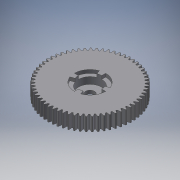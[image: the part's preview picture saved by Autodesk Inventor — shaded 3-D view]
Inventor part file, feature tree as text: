
AUTODESK INVENTOR PART (.ipt)
format: ipt  version: 2017 (Build 210142000, 142)  size: 384,000 bytes
history: native  units: mm
features: extrude x5, sketch x4, pattern_circular x2
ambient origin geometry x8: Origin, YZ Plane, XZ Plane, XY Plane, X Axis, Y Axis, Z Axis, Center Point
bodies: Solid1 (feature_tree)
feature tree (11):
  sketch  "Sketch1"  dims[d0=20.0mm d1=0.0mm]
  extrude  "Extrusion1"  TaperAngle=0.0deg  [1 undecoded]
  extrude  "Extrusion2"  Depth=10.0mm TaperAngle=360.0deg
  pattern_circular  "Circular Pattern1"  [2 undecoded]
  extrude  "Extrusion3"  Depth=15.0mm TaperAngle=0.0deg
  extrude  "Extrusion4"  Depth=5.0mm
  extrude  "Extrusion5"  Depth=5.0mm
  pattern_circular  "Circular Pattern2"  [2 undecoded]
  sketch  "Sketch2"  dims[d2=10.0mm d3=0.0mm d4=610.0mm d5=360.0deg]
  sketch  "Sketch3"  dims[d7=13.5mm]
  sketch  "Sketch4"  dims[d8=10.0mm d9=0.0mm d10=35.0mm d11=15.0mm d12=0.0mm d13=6.0mm d14=12.217305mm d15=5.0mm d16=0.0mm d17=40.0mm d18=360.0deg]
note: 5 required parameter values undecoded (feature->parameter linkage not recoverable at this tier; creation-order binding heuristic only, values carry confidence <= 0.55)
